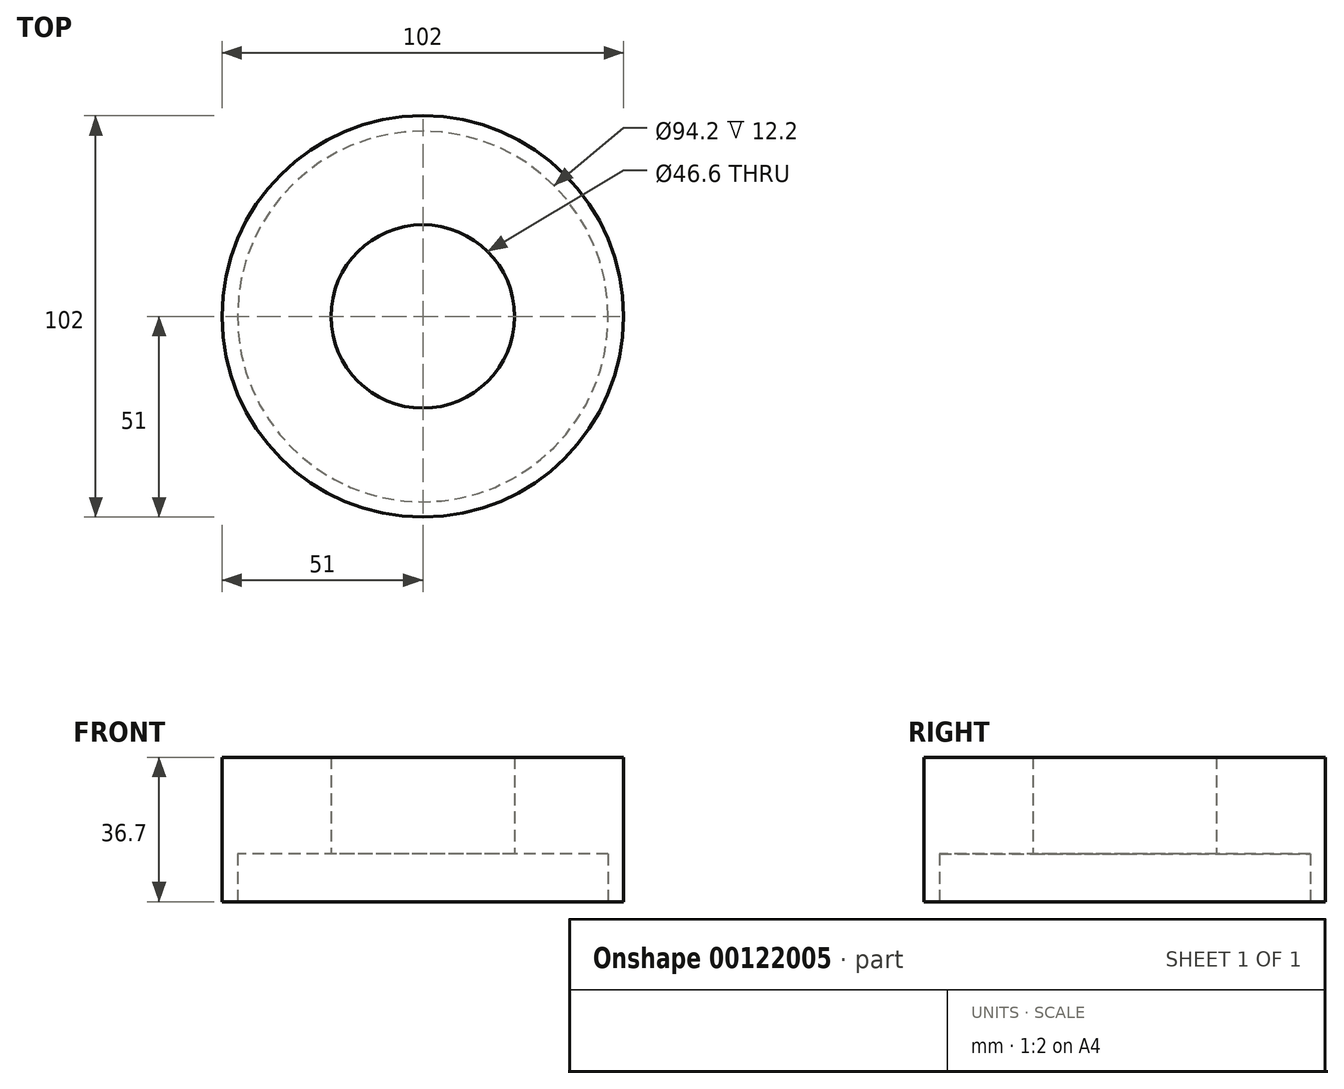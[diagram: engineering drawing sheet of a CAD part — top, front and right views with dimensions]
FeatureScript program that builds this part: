
annotation { "Feature Type Name" : "Feature", "Feature Type Description" : "" }
export const myFeature = defineFeature(function(context is Context, id is Id, definition is map)
    precondition{}
    {
        {
            var Q0;
            Q0=qCreatedBy(makeId("Top.planeOp"),FACE);
            var sketch = newSketch(context, id + "F0", { "sketchPlane" : qUnion([Q0])});
            skCircle(sketch, "E0", {"center": v(0, 0) * mm, "radius": 51 * mm});
            skSolve(sketch);
        }
        {
            var Q0;
            Q0=makeQuery(id+"F0.imprint","IMPRINT",FACE,{"disambiguationData":[TD([[makeQuery(id+"F0.imprint","IMPRINT",EDGE,{"derivedFrom":sQuery(id+"F0.wireOp",EDGE,"E0")}),1.0]])]});
            extrude(context, id + "F1", {"entities" : qUnion([Q0]), "depth" : 36.7 * mm});
        }
        {
            var Q0;
            Q0=qCreatedBy(makeId("Top.planeOp"),FACE);
            var sketch = newSketch(context, id + "F2", { "sketchPlane" : qUnion([Q0])});
            skCircle(sketch, "E1", {"center": v(0, 0) * mm, "radius": 47.1 * mm});
            skSolve(sketch);
        }
        {
            var Q0;
            Q0 = qSketchRegion(id + "F2", true);
            var Q1;
            Q1=sQuery(id+"F2.wireOp",EDGE,"E1");
            extrude(context, id + "F3", {"entities" : qUnion([Q0]), "operationType" : NewBodyOperationType.REMOVE, "surfaceEntities" : qUnion([Q1]), "depth" : 12.2 * mm});
        }
        {
            var Q0;
            Q0=qCreatedBy(makeId("Top.planeOp"),FACE);
            var sketch = newSketch(context, id + "F4", { "sketchPlane" : qUnion([Q0])});
            skCircle(sketch, "E2", {"center": v(0, 0) * mm, "radius": 23.3 * mm});
            skSolve(sketch);
        }
        {
            var Q0;
            Q0 = qSketchRegion(id + "F4", true);
            extrude(context, id + "F5", {"entities" : qUnion([Q0]), "operationType" : NewBodyOperationType.REMOVE, "depth" : 85 * mm});
        }
    });
